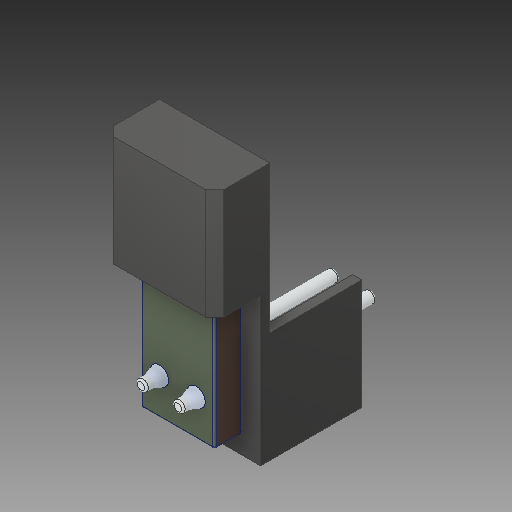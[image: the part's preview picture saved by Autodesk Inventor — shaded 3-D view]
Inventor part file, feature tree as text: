
AUTODESK INVENTOR PART (.ipt)
format: ipt  version: 2019 (Build 230136000, 136)  size: 178,176 bytes
history: mixed  units: mm
features: other x10, fillet x3, chamfer x1, imported_body x1
ambient origin geometry x8: Origin, YZ Plane, XZ Plane, XY Plane, X Axis, Y Axis, Z Axis, Center Point
bodies: Body1 (imported_parasolid), Body2 (imported_parasolid), Body3 (imported_parasolid), Body4 (imported_parasolid), Body5 (imported_parasolid), Body6 (imported_parasolid), Body7 (imported_parasolid)
feature tree (15):
  other  "Твердое тело1"
  other  "Твердое тело2"
  other  "Твердое тело3"
  other  "Твердое тело4"
  other  "Твердое тело5"
  other  "Твердое тело6"
  other  "Твердое тело7"
  chamfer  "Chamfer1"  [1 undecoded]
  other  "Dome1"
  fillet  "Fillet2"  [1 undecoded]
  fillet  "Fillet4"  [1 undecoded]
  fillet  "Fillet5"  [1 undecoded]
  other  "Boss-Extrude9[1]"
  other  "Boss-Extrude9[2]"
  imported_body  NMx_Import_Brep_tag  [imported B-rep: ~60 faces, bbox_mm=[6.0, 14.0, 10.5]]
note: 4 required parameter values undecoded (feature->parameter linkage not recoverable at this tier; creation-order binding heuristic only, values carry confidence <= 0.55)
